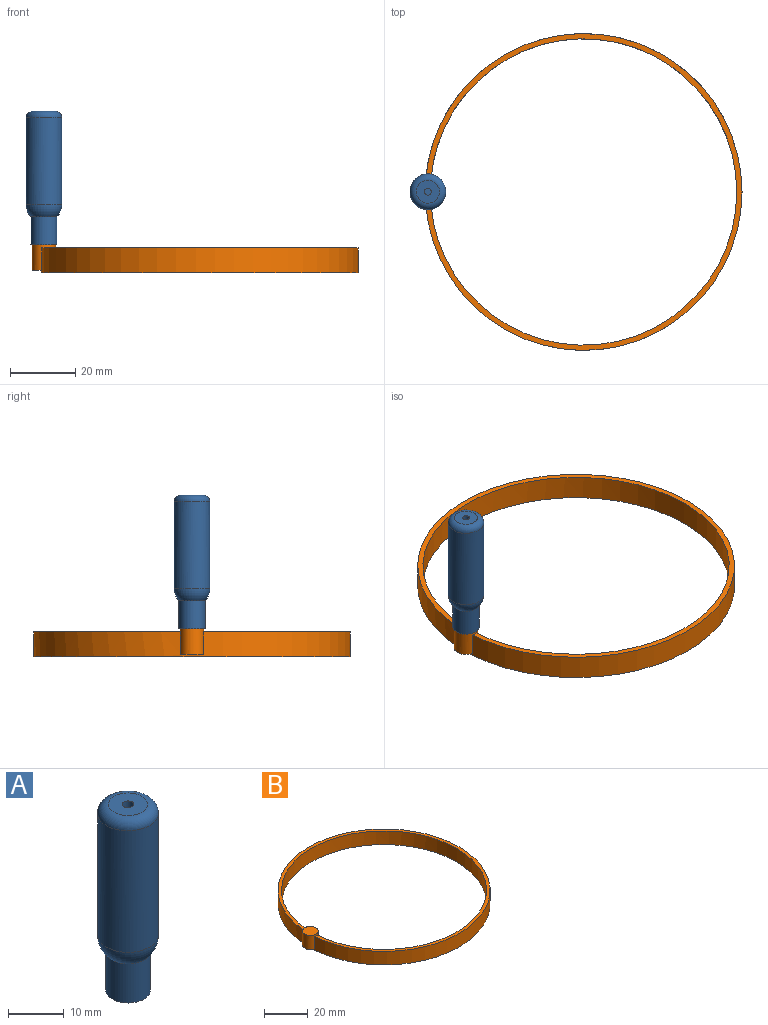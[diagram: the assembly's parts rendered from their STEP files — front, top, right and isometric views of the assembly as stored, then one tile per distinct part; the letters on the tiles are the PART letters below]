
ASSEMBLY  parts=2 mates=1
PART A: 8 faces, bbox 11.9x11.9x40.9 mm
  f0: cylinder r=4.02mm len=8.64mm, axis (0,0,1), area 218.2mm2, adj f1,f7
  f1: plane 8.04x8.04mm, normal (0,0,-1), area 50.8mm2, adj f0
  f2: plane 7.05x7.05mm, normal (0,0,1), area 35.6mm2, adj f4,f6
  f3: cylinder r=5.49mm len=26.78mm, axis (0,0,1), area 923.2mm2, adj f6,f7
  f4: cylinder r=1.04mm len=11.23mm, axis (0,0,1), area 73.4mm2, adj f2,f5
  f5: plane 2.08x2.08mm, normal (0,0,1), area 3.4mm2, adj f4
  f6: torus R=3.52mm, axis (0,0,1), area 92.4mm2, adj f2,f3
  f7: torus R=0.41mm, axis (0,0,-1), area 124mm2, adj f0,f3
PART B: 8 faces, bbox 100x97.2x8.6 mm
  f0: cylinder r=47.01mm len=94.02mm, axis (0,0,-1), area 2202.6mm2, adj f2,f3,f4,f5
  f1: cylinder r=48.62mm len=97.24mm, axis (0,0,-1), area 2278.9mm2, adj f2,f3,f5,f6
  f2: plane 97.24x97.11mm, normal (0,0,1), area 471mm2, adj f0,f1,f5
  f3: plane 97.24x97.24mm, normal (0,0,-1), area 482.5mm2, adj f0,f1
  f4: plane 7.02x2.85mm, normal (0,0,-1), area 14.8mm2, adj f0,f5
  f5: cylinder r=3.63mm len=7.87mm, axis (0,0,1), area 157.1mm2, adj f0,f1,f2,f4,f6,f7
  f6: plane 7.11x2.93mm, normal (0,0,-1), area 15mm2, adj f1,f5
  f7: plane 7.25x7.25mm, normal (0,0,1), area 41.3mm2, adj f5
PLACE A t=(-98.89,-6.17,-6.6)mm
PLACE B t=(-51.1,-6.17,-1.27)mm
MATE fastened B.f5 <-> A.f0  axis (0,0,1) through (-98.89,-6.17,-15.24)mm
